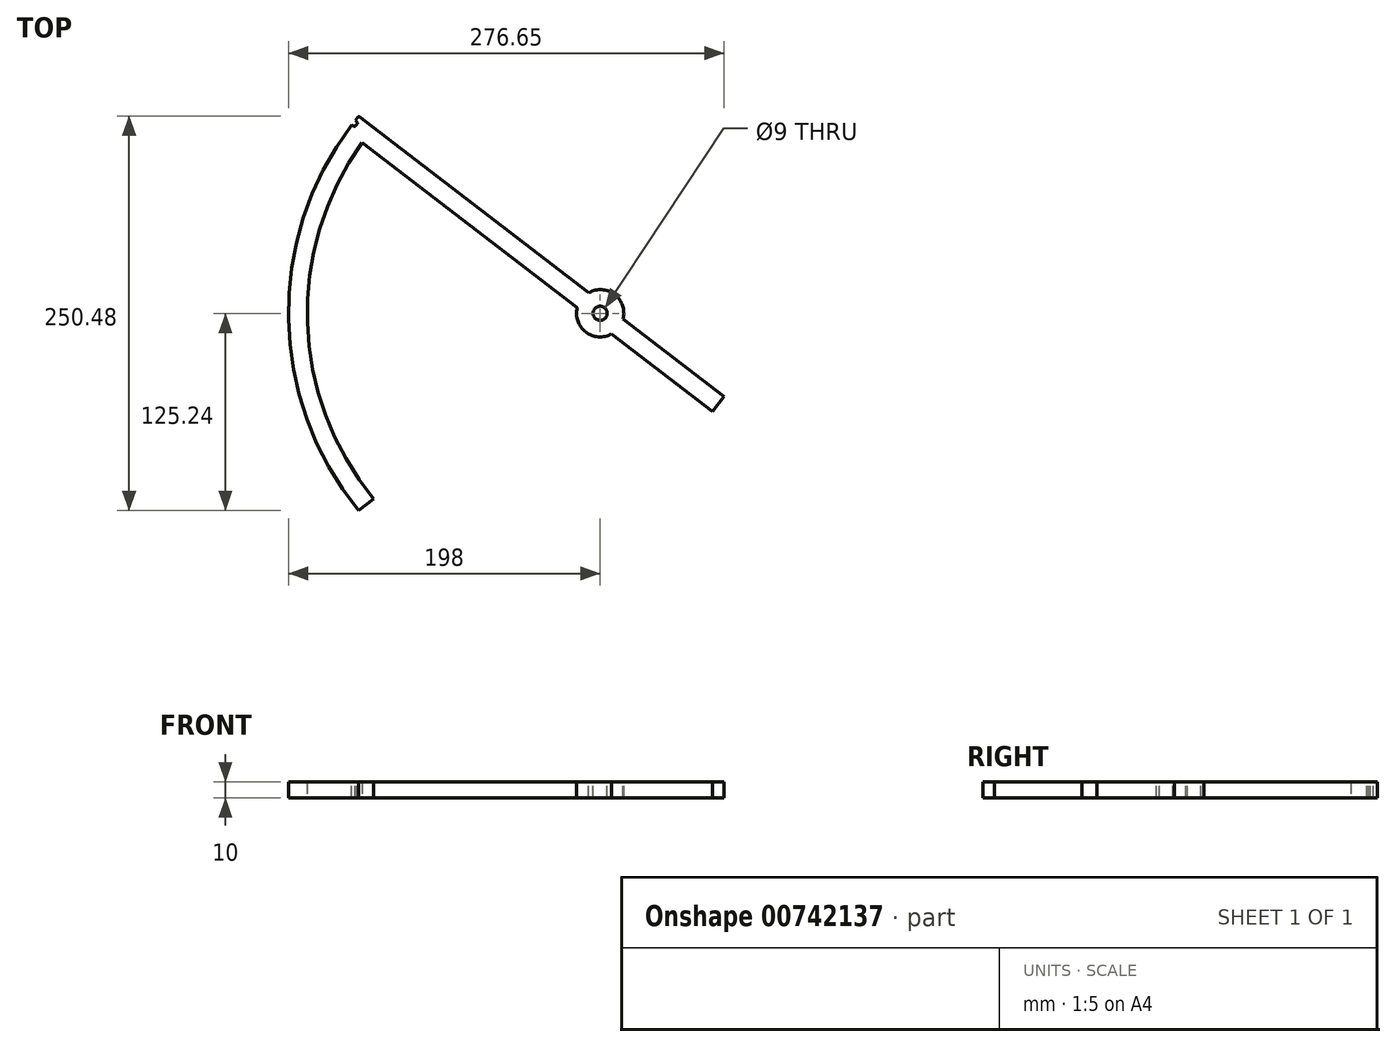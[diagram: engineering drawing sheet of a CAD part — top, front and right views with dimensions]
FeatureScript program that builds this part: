
annotation { "Feature Type Name" : "Feature", "Feature Type Description" : "" }
export const myFeature = defineFeature(function(context is Context, id is Id, definition is map)
    precondition{}
    {
        {
            var Q0;
            Q0=qCreatedBy(makeId("Top.planeOp"),FACE);
            var sketch = newSketch(context, id + "F0", { "sketchPlane" : qUnion([Q0])});
            skLineSegment(sketch, "E0", {"start": v(75, -57.55) * mm, "end": v(-152.32, 116.88) * mm});
            skArc(sketch, "E1", {"start": v(-152.32, 116.88) * mm, "mid": v(-191.98, -3) * mm, "end": v(-148.6, -121.59) * mm});
            skLineSegment(sketch, "E2", {"start": v(71.35, -62.3) * mm, "end": v(78.65, -52.79) * mm});
            skLineSegment(sketch, "E3", {"start": v(78.65, -52.79) * mm, "end": v(-153.36, 125.24) * mm});
            skArc(sketch, "E4", {"start": v(-153.36, 125.24) * mm, "mid": v(-198, 0) * mm, "end": v(-153.36, -125.24) * mm});
            skLineSegment(sketch, "E5", {"start": v(-153.36, -125.24) * mm, "end": v(-143.83, -117.93) * mm});
            skArc(sketch, "E6", {"start": v(-151.14, 108.41) * mm, "mid": v(-185.9, -6) * mm, "end": v(-143.83, -117.93) * mm});
            skLineSegment(sketch, "E7", {"start": v(-151.14, 108.41) * mm, "end": v(71.35, -62.3) * mm});
            skSolve(sketch);
        }
        {
            var Q0;
            {var subQ2=sQuery(id+"F0.wireOp",EDGE,"E0");Q0=makeQuery(id+"F0.imprint","IMPRINT",FACE,{"disambiguationData":[TD([[makeQuery(id+"F0.imprint","IMPRINT",EDGE,{"derivedFrom":subQ2}),-1.0]])]});}
            var Q1;
            {var subQ4=sQuery(id+"F0.wireOp",EDGE,"E0");Q1=makeQuery(id+"F0.imprint","IMPRINT",FACE,{"disambiguationData":[TD([[makeQuery(id+"F0.imprint","IMPRINT",EDGE,{"derivedFrom":subQ4}),1.0]])]});}
            extrude(context, id + "F1", {"entities" : qUnion([Q0, Q1]), "depth" : 10 * mm, "offsetDistance" : 25 * mm});
        }
        {
            var Q0;
            Q0=makeQuery(id+"F1.opExtrude","CAP_FACE",FACE,{"disambiguationData":[OSD([sQuery(id+"F0.wireOp",EDGE,"E2"),sQuery(id+"F0.wireOp",EDGE,"E3"),sQuery(id+"F0.wireOp",EDGE,"E4"),sQuery(id+"F0.wireOp",EDGE,"E5"),sQuery(id+"F0.wireOp",EDGE,"E6"),sQuery(id+"F0.wireOp",EDGE,"E7")])],"isStart":false});
            var sketch = newSketch(context, id + "F2", { "sketchPlane" : qUnion([Q0])});
            skCircle(sketch, "E8", {"center": v(0, 0) * mm, "radius": 15 * mm});
            skSolve(sketch);
        }
        {
            var Q0;
            {var subQ0=sQuery(id+"F2.wireOp",EDGE,"E8");var subQ1=makeQuery(id+"F1.opExtrude","CAP_EDGE",EDGE,{"disambiguationData":[OSD([sQuery(id+"F0.wireOp",EDGE,"E3")])],"isStart":false});var subQ2=makeQuery(id+"F2.imprint","INTERSECT",VERTEX,{"disambiguationData":[OD(0.0)],"derivedFrom":[subQ1,subQ0]});Q0=makeQuery(id+"F2.imprint","IMPRINT",FACE,{"disambiguationData":[TD([[makeQuery(id+"F2.imprint","IMPRINT",EDGE,{"disambiguationData":[TD([[subQ2,1.0]])],"derivedFrom":subQ0}),1.0]])]});}
            var Q1;
            {var subQ0=sQuery(id+"F2.wireOp",EDGE,"E8");var subQ1=makeQuery(id+"F1.opExtrude","CAP_EDGE",EDGE,{"disambiguationData":[OSD([sQuery(id+"F0.wireOp",EDGE,"E7")])],"isStart":false});var subQ2=makeQuery(id+"F2.imprint","INTERSECT",VERTEX,{"disambiguationData":[OD(0.0)],"derivedFrom":[subQ1,subQ0]});Q1=makeQuery(id+"F2.imprint","IMPRINT",FACE,{"disambiguationData":[TD([[makeQuery(id+"F2.imprint","IMPRINT",EDGE,{"disambiguationData":[TD([[subQ2,-1.0]])],"derivedFrom":subQ0}),1.0]])]});}
            var Q2;
            {var subQ0=sQuery(id+"F2.wireOp",EDGE,"E8");var subQ1=makeQuery(id+"F1.opExtrude","CAP_EDGE",EDGE,{"disambiguationData":[OSD([sQuery(id+"F0.wireOp",EDGE,"E7")])],"isStart":false});var subQ2=makeQuery(id+"F2.imprint","INTERSECT",VERTEX,{"disambiguationData":[OD(0.0)],"derivedFrom":[subQ1,subQ0]});Q2=makeQuery(id+"F2.imprint","IMPRINT",FACE,{"disambiguationData":[TD([[makeQuery(id+"F2.imprint","IMPRINT",EDGE,{"disambiguationData":[TD([[subQ2,1.0]])],"derivedFrom":subQ0}),1.0]])]});}
            extrude(context, id + "F3", {"entities" : qUnion([Q0, Q1, Q2]), "operationType" : NewBodyOperationType.ADD, "oppositeDirection" : true, "depth" : 10 * mm, "offsetDistance" : 25 * mm});
        }
        {
            var Q0;
            Q0=makeQuery(id+"F3.boolean.opBoolean","MERGE",FACE,{"derivedFrom":[makeQuery(id+"F1.opExtrude","CAP_FACE",FACE,{"disambiguationData":[OSD([sQuery(id+"F0.wireOp",EDGE,"E2"),sQuery(id+"F0.wireOp",EDGE,"E3"),sQuery(id+"F0.wireOp",EDGE,"E4"),sQuery(id+"F0.wireOp",EDGE,"E5"),sQuery(id+"F0.wireOp",EDGE,"E6"),sQuery(id+"F0.wireOp",EDGE,"E7")])],"isStart":false}),makeQuery(id+"F3.opExtrude","CAP_FACE",FACE,{"disambiguationData":[OSD([sQuery(id+"F2.wireOp",EDGE,"E8")])],"isStart":true})]});
            var sketch = newSketch(context, id + "F4", { "sketchPlane" : qUnion([Q0])});
            skCircle(sketch, "E9", {"center": v(0, 0) * mm, "radius": 4.5 * mm});
            skSolve(sketch);
        }
        {
            var Q0;
            Q0=makeQuery(id+"F4.imprint","IMPRINT",FACE,{"disambiguationData":[TD([[makeQuery(id+"F4.imprint","IMPRINT",EDGE,{"derivedFrom":sQuery(id+"F4.wireOp",EDGE,"E9")}),1.0]])]});
            extrude(context, id + "F5", {"entities" : qUnion([Q0]), "operationType" : NewBodyOperationType.REMOVE, "endBound" : BoundingType.THROUGH_ALL, "oppositeDirection" : true, "depth" : 25 * mm, "offsetDistance" : 25 * mm});
        }
        {
            var Q0;
            Q0=makeQuery(id+"F3.boolean.opBoolean","MERGE",FACE,{"derivedFrom":[makeQuery(id+"F1.opExtrude","CAP_FACE",FACE,{"disambiguationData":[OSD([sQuery(id+"F0.wireOp",EDGE,"E2"),sQuery(id+"F0.wireOp",EDGE,"E3"),sQuery(id+"F0.wireOp",EDGE,"E4"),sQuery(id+"F0.wireOp",EDGE,"E5"),sQuery(id+"F0.wireOp",EDGE,"E6"),sQuery(id+"F0.wireOp",EDGE,"E7")])],"isStart":false}),makeQuery(id+"F3.opExtrude","CAP_FACE",FACE,{"disambiguationData":[OSD([sQuery(id+"F2.wireOp",EDGE,"E8")])],"isStart":true})]});
            var sketch = newSketch(context, id + "F6", { "sketchPlane" : qUnion([Q0])});
            skArc(sketch, "E10", {"start": v(-152.57, 124.63) * mm, "mid": v(-197, 0) * mm, "end": v(-152.57, -124.63) * mm, "construction": true});
            skArc(sketch, "E11", {"start": v(-151.57, 123.87) * mm, "mid": v(-195.75, 0) * mm, "end": v(-151.57, -123.87) * mm});
            skLineSegment(sketch, "E12", {"start": v(-151.57, 123.87) * mm, "end": v(-153.65, 124.89) * mm});
            skLineSegment(sketch, "E13", {"start": v(-155.44, 122.65) * mm, "end": v(-154, 120.85) * mm});
            skLineSegment(sketch, "E14", {"start": v(-155.74, 118.58) * mm, "end": v(-154, 120.85) * mm});
            skLineSegment(sketch, "E15", {"start": v(-155.44, 122.65) * mm, "end": v(-153.65, 124.89) * mm});
            skLineSegment(sketch, "E16", {"start": v(-155.74, 118.58) * mm, "end": v(0, 0) * mm, "construction": true});
            skLineSegment(sketch, "E17", {"start": v(-155.44, 122.65) * mm, "end": v(0, 0) * mm, "construction": true});
            skLineSegment(sketch, "E18", {"start": v(-153.65, 124.89) * mm, "end": v(0, 0) * mm, "construction": true});
            skLineSegment(sketch, "E19", {"start": v(-155.74, 118.58) * mm, "end": v(-157.8, 119.6) * mm});
            skSolve(sketch);
        }
        {
            var Q0;
            {var subQ1=sQuery(id+"F6.wireOp",EDGE,"E13");Q0=makeQuery(id+"F6.imprint","IMPRINT",FACE,{"disambiguationData":[TD([[makeQuery(id+"F6.imprint","IMPRINT",EDGE,{"derivedFrom":subQ1}),-1.0]])]});}
            extrude(context, id + "F7", {"entities" : qUnion([Q0]), "operationType" : NewBodyOperationType.REMOVE, "oppositeDirection" : true, "depth" : 25 * mm, "offsetDistance" : 25 * mm});
        }
    });
